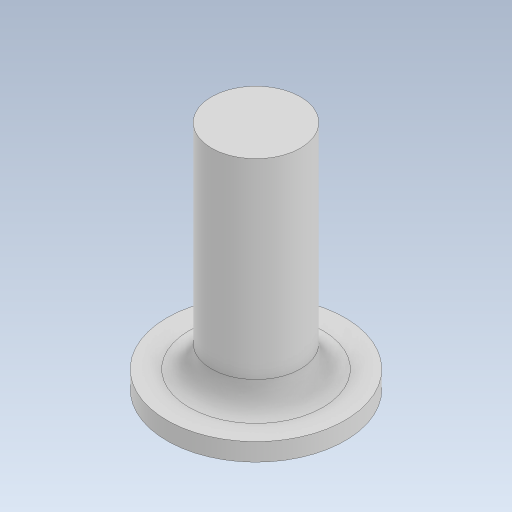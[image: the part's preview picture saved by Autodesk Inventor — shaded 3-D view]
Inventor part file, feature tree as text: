
AUTODESK INVENTOR PART (.ipt)
format: ipt  version: 2023 (Build 270158000, 158)  size: 115,712 bytes
history: native  units: in
note: dims shown in document units (in); Inventor stores cm internally (conversion verified against a paired STEP export)
features: extrude x2, sketch x1, fillet x1
ambient origin geometry x8: Origin, YZ Plane, XZ Plane, XY Plane, X Axis, Y Axis, Z Axis, Center Point
bodies: Solid1 (feature_tree)
feature tree (4):
  sketch  "Sketch1"  dims[d0=0.5in d1=0.25in d2=0.6in d3=0.0in d4=0.05in d5=0.0in d6=0.0625in]
  extrude  "Extrusion1"  Depth=0.25in
  extrude  "Extrusion2"  Depth=0.6in TaperAngle=0.0deg
  fillet  "Fillet1"  Radius=0.05in
